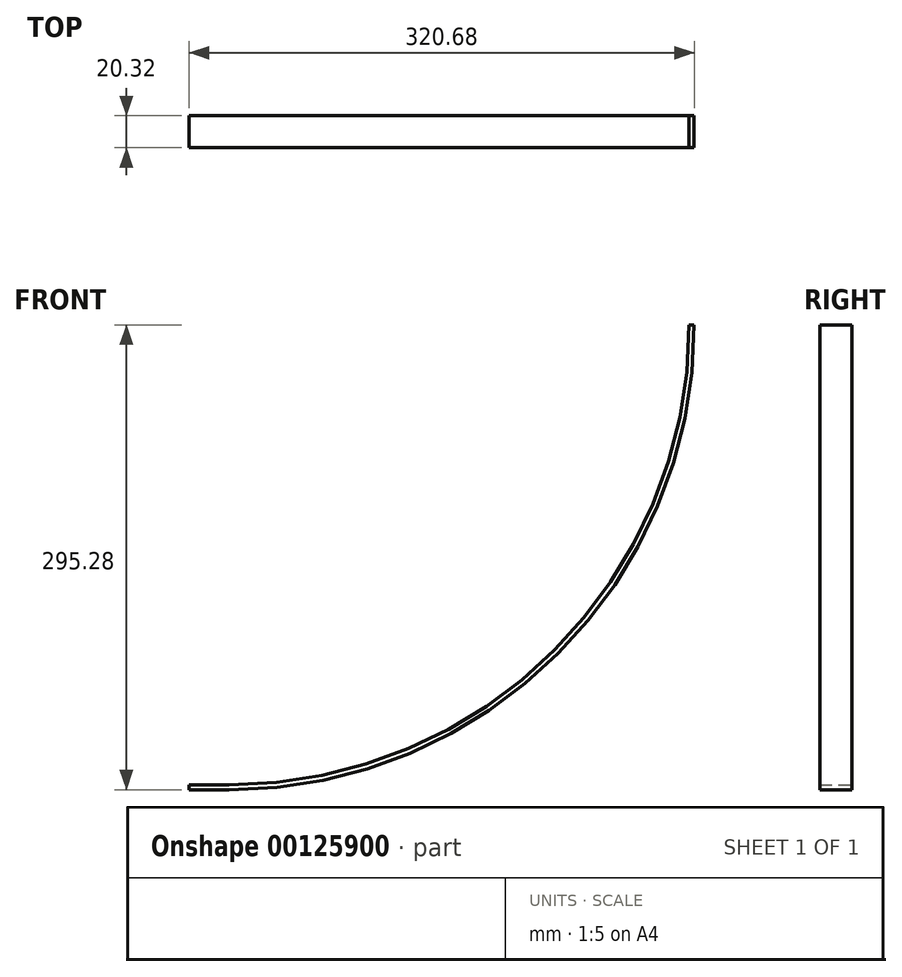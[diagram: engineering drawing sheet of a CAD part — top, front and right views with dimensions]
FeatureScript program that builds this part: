
annotation { "Feature Type Name" : "Feature", "Feature Type Description" : "" }
export const myFeature = defineFeature(function(context is Context, id is Id, definition is map)
    precondition{}
    {
        {
            var Q0;
            Q0=qCreatedBy(makeId("Front.planeOp"),FACE);
            var sketch = newSketch(context, id + "F0", { "sketchPlane" : qUnion([Q0])});
            skArc(sketch, "E0", {"start": v(0, -292.1) * mm, "mid": v(292.1, 0) * mm, "end": v(0, 292.1) * mm});
            skArc(sketch, "E1.0", {"start": v(0, -295.28) * mm, "mid": v(295.28, 0) * mm, "end": v(0, 295.28) * mm});
            skLineSegment(sketch, "E2", {"start": v(0, 295.28) * mm, "end": v(0, -295.28) * mm, "construction": true});
            skLineSegment(sketch, "E3", {"start": v(0, 295.28) * mm, "end": v(0, 292.1) * mm});
            skLineSegment(sketch, "E4", {"start": v(0, -295.28) * mm, "end": v(0, -292.1) * mm});
            skLineSegment(sketch, "E5", {"start": v(5.76, 0) * mm, "end": v(295.28, 0) * mm, "construction": true});
            skLineSegment(sketch, "E6", {"start": v(295.28, 0) * mm, "end": v(292.1, 0) * mm});
            skSolve(sketch);
        }
        {
            var Q0;
            {var subQ0=sQuery(id+"F0.wireOp",EDGE,"E4");Q0=makeQuery(id+"F0.imprint","IMPRINT",FACE,{"disambiguationData":[TD([[makeQuery(id+"F0.imprint","IMPRINT",EDGE,{"derivedFrom":subQ0}),-1.0]])]});}
            extrude(context, id + "F1", {"entities" : qUnion([Q0]), "depth" : 20.32 * mm});
        }
        {
            var Q0;
            Q0=makeQuery(id+"F1.opExtrude","SWEPT_FACE",FACE,{"disambiguationData":[OSD([sQuery(id+"F0.wireOp",EDGE,"E4")])]});
            var sketch = newSketch(context, id + "F2", { "sketchPlane" : qUnion([Q0])});
            skLineSegment(sketch, "E7.bottom", {"start": v(0, -292.1) * mm, "end": v(20.32, -292.1) * mm});
            skLineSegment(sketch, "E7.top", {"start": v(0, -295.28) * mm, "end": v(20.32, -295.28) * mm});
            skLineSegment(sketch, "E7.left", {"start": v(0, -292.1) * mm, "end": v(0, -295.28) * mm});
            skLineSegment(sketch, "E7.right", {"start": v(20.32, -292.1) * mm, "end": v(20.32, -295.28) * mm});
            skSolve(sketch);
        }
        {
            var Q0;
            Q0=makeQuery(id+"F2.imprint","IMPRINT",FACE,{"disambiguationData":[TD([[makeQuery(id+"F2.imprint","IMPRINT",EDGE,{"derivedFrom":sQuery(id+"F2.wireOp",EDGE,"E7.bottom")}),1.0]])]});
            extrude(context, id + "F3", {"entities" : qUnion([Q0]), "operationType" : NewBodyOperationType.ADD, "depth" : 25.4 * mm});
        }
    });
